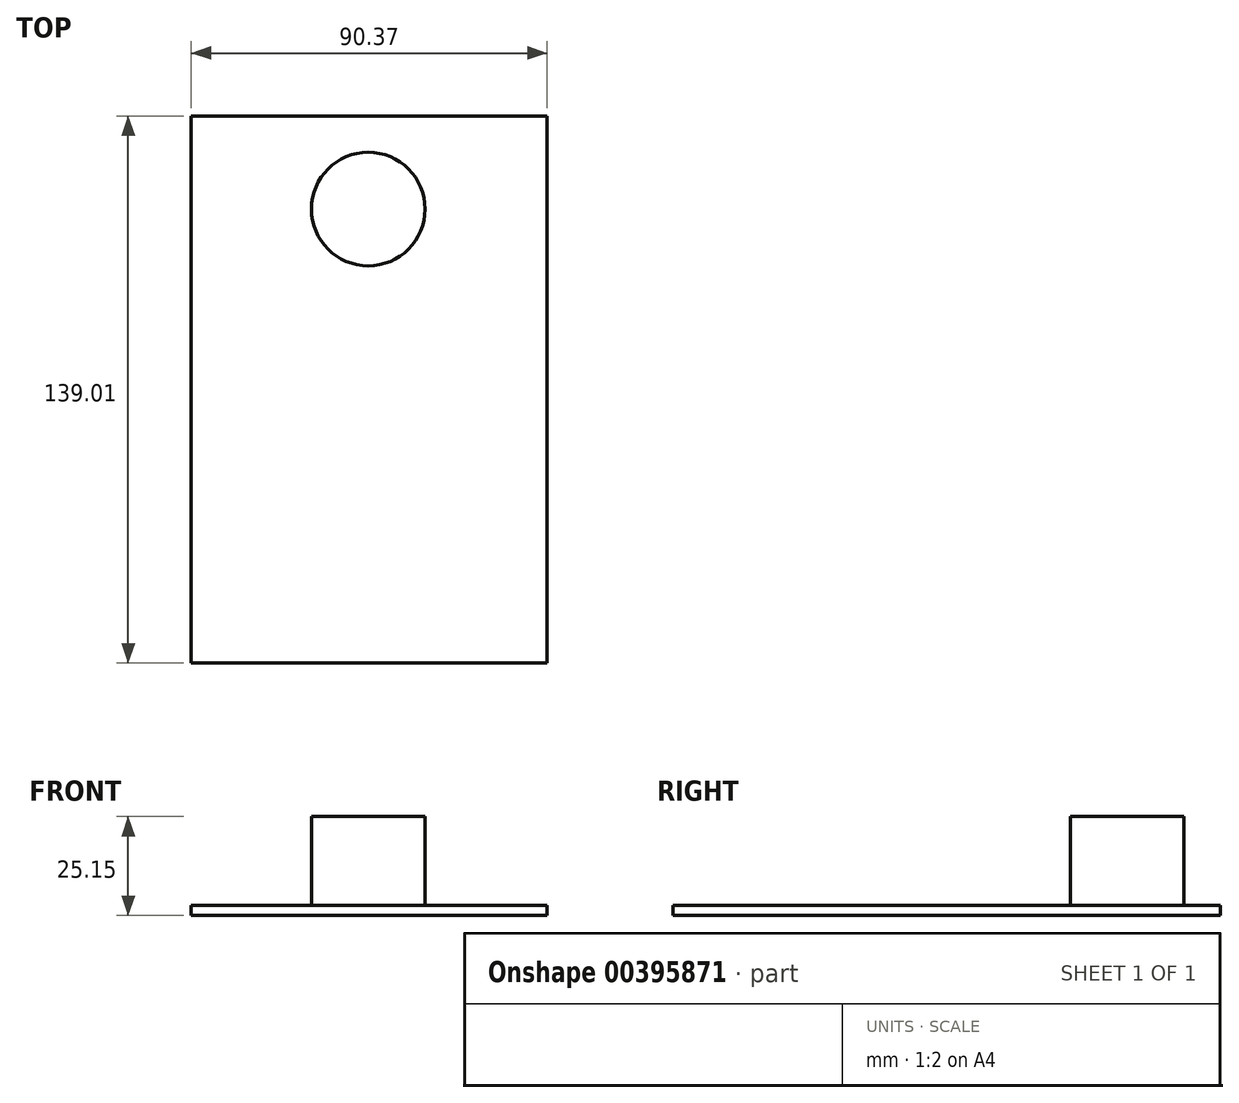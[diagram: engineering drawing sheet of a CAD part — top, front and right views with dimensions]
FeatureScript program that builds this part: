
annotation { "Feature Type Name" : "Feature", "Feature Type Description" : "" }
export const myFeature = defineFeature(function(context is Context, id is Id, definition is map)
    precondition{}
    {
        {
            var Q0;
            Q0=qCreatedBy(makeId("Top.planeOp"),FACE);
            var sketch = newSketch(context, id + "F0", { "sketchPlane" : qUnion([Q0])});
            skLineSegment(sketch, "E0.bottom", {"start": v(31.66, 60.15) * mm, "end": v(-58.71, 60.15) * mm});
            skLineSegment(sketch, "E0.top", {"start": v(31.66, -78.86) * mm, "end": v(-58.71, -78.86) * mm});
            skLineSegment(sketch, "E0.left", {"start": v(31.66, 60.15) * mm, "end": v(31.66, -78.86) * mm});
            skLineSegment(sketch, "E0.right", {"start": v(-58.71, 60.15) * mm, "end": v(-58.71, -78.86) * mm});
            skSolve(sketch);
        }
        {
            var Q0;
            Q0 = qSketchRegion(id + "F0", true);
            extrude(context, id + "F1", {"entities" : qUnion([Q0]), "oppositeDirection" : true, "depth" : 2.54 * mm});
        }
        {
            var Q0;
            Q0=makeQuery(id+"F1.opExtrude","CAP_FACE",FACE,{"disambiguationData":[OSD([sQuery(id+"F0.wireOp",EDGE,"E0.bottom"),sQuery(id+"F0.wireOp",EDGE,"E0.top"),sQuery(id+"F0.wireOp",EDGE,"E0.left"),sQuery(id+"F0.wireOp",EDGE,"E0.right")])],"isStart":true});
            shell(context, id + "F2", {"entities" : qUnion([Q0]), "thickness" : 2.54 * mm});
        }
        {
            var Q0;
            Q0=makeQuery(id+"F1.opExtrude","CAP_FACE",FACE,{"disambiguationData":[OSD([sQuery(id+"F0.wireOp",EDGE,"E0.bottom"),sQuery(id+"F0.wireOp",EDGE,"E0.top"),sQuery(id+"F0.wireOp",EDGE,"E0.left"),sQuery(id+"F0.wireOp",EDGE,"E0.right")])],"isStart":true});
            var sketch = newSketch(context, id + "F3", { "sketchPlane" : qUnion([Q0])});
            skCircle(sketch, "E1", {"center": v(-13.76, 36.5) * mm, "radius": 14.43 * mm});
            skSolve(sketch);
        }
        {
            var Q0;
            Q0 = qSketchRegion(id + "F3", true);
            extrude(context, id + "F4", {"entities" : qUnion([Q0]), "operationType" : NewBodyOperationType.ADD, "depth" : 22.6 * mm});
        }
    });
